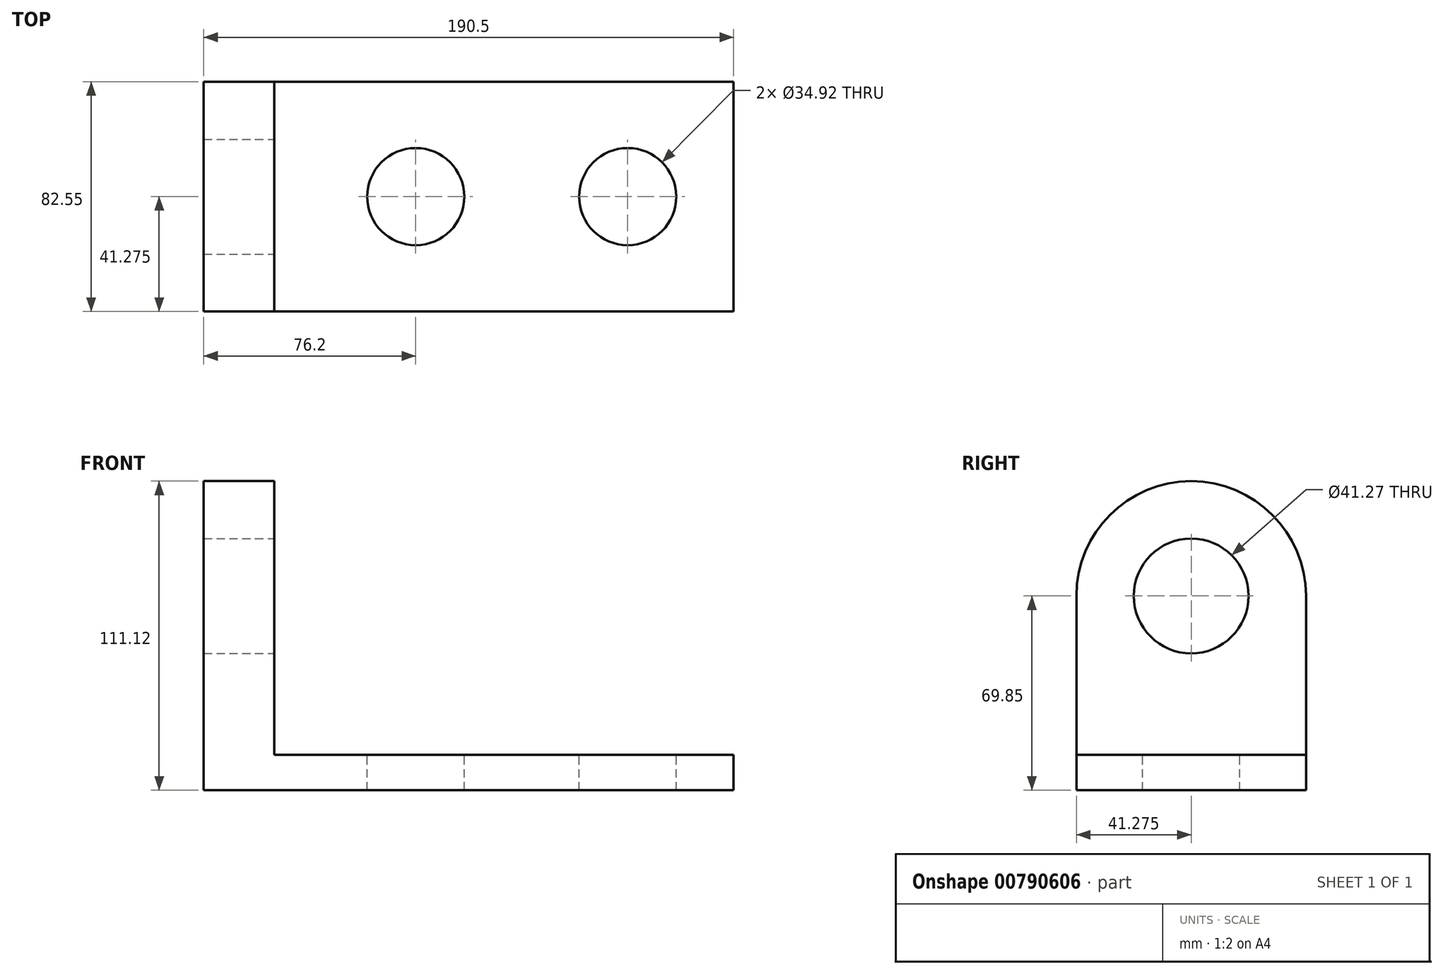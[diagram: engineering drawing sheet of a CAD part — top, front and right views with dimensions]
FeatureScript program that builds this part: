
annotation { "Feature Type Name" : "Feature", "Feature Type Description" : "" }
export const myFeature = defineFeature(function(context is Context, id is Id, definition is map)
    precondition{}
    {
        {
            var Q0;
            Q0=qCreatedBy(makeId("Front.planeOp"),FACE);
            var sketch = newSketch(context, id + "F0", { "sketchPlane" : qUnion([Q0])});
            skLineSegment(sketch, "E0", {"start": v(0, 0) * mm, "end": v(190.5, 0) * mm});
            skLineSegment(sketch, "E1", {"start": v(190.5, 0) * mm, "end": v(190.5, 12.7) * mm});
            skLineSegment(sketch, "E2", {"start": v(190.5, 12.7) * mm, "end": v(0, 12.7) * mm});
            skLineSegment(sketch, "E3", {"start": v(0, 12.7) * mm, "end": v(0, 0) * mm});
            skSolve(sketch);
        }
        {
            var Q0;
            Q0=makeQuery(id+"F0.imprint","IMPRINT",FACE,{"disambiguationData":[TD([[makeQuery(id+"F0.imprint","IMPRINT",EDGE,{"derivedFrom":sQuery(id+"F0.wireOp",EDGE,"E0")}),1.0]])]});
            extrude(context, id + "F1", {"entities" : qUnion([Q0]), "depth" : 82.55 * mm, "offsetDistance" : 25.4 * mm});
        }
        {
            var Q0;
            Q0=makeQuery(id+"F1.opExtrude","SWEPT_FACE",FACE,{"disambiguationData":[OSD([sQuery(id+"F0.wireOp",EDGE,"E2")])]});
            var sketch = newSketch(context, id + "F2", { "sketchPlane" : qUnion([Q0])});
            skLineSegment(sketch, "E4", {"start": v(190.5, -41.28) * mm, "end": v(152.4, -41.28) * mm, "construction": true});
            skLineSegment(sketch, "E5", {"start": v(152.4, -41.28) * mm, "end": v(76.2, -41.28) * mm, "construction": true});
            skCircle(sketch, "E6", {"center": v(76.2, -41.28) * mm, "radius": 17.46 * mm});
            skCircle(sketch, "E7", {"center": v(152.4, -41.28) * mm, "radius": 17.46 * mm});
            skSolve(sketch);
        }
        {
            var Q0;
            Q0=makeQuery(id+"F2.imprint","IMPRINT",FACE,{"disambiguationData":[TD([[makeQuery(id+"F2.imprint","IMPRINT",EDGE,{"derivedFrom":sQuery(id+"F2.wireOp",EDGE,"E6")}),1.0]])]});
            var Q1;
            Q1=makeQuery(id+"F2.imprint","IMPRINT",FACE,{"disambiguationData":[TD([[makeQuery(id+"F2.imprint","IMPRINT",EDGE,{"derivedFrom":sQuery(id+"F2.wireOp",EDGE,"E7")}),1.0]])]});
            extrude(context, id + "F3", {"entities" : qUnion([Q0, Q1]), "operationType" : NewBodyOperationType.REMOVE, "oppositeDirection" : true, "depth" : 25.4 * mm, "offsetDistance" : 25.4 * mm});
        }
        {
            var Q0;
            Q0=makeQuery(id+"F1.opExtrude","CAP_FACE",FACE,{"disambiguationData":[OSD([sQuery(id+"F0.wireOp",EDGE,"E0"),sQuery(id+"F0.wireOp",EDGE,"E1"),sQuery(id+"F0.wireOp",EDGE,"E2"),sQuery(id+"F0.wireOp",EDGE,"E3")])],"isStart":false});
            var sketch = newSketch(context, id + "F4", { "sketchPlane" : qUnion([Q0])});
            skLineSegment(sketch, "E8", {"start": v(0, 0) * mm, "end": v(25.4, 0) * mm});
            skLineSegment(sketch, "E9", {"start": v(0, 0) * mm, "end": v(0, 114.3) * mm});
            skLineSegment(sketch, "E10", {"start": v(25.4, 0) * mm, "end": v(25.4, 114.3) * mm});
            skLineSegment(sketch, "E11", {"start": v(25.4, 114.3) * mm, "end": v(0, 114.3) * mm});
            skSolve(sketch);
        }
        {
            var Q0;
            {var subQ3=sQuery(id+"F4.wireOp",EDGE,"E11");Q0=makeQuery(id+"F4.imprint","IMPRINT",FACE,{"disambiguationData":[TD([[makeQuery(id+"F4.imprint","IMPRINT",EDGE,{"derivedFrom":subQ3}),1.0]])]});}
            extrude(context, id + "F5", {"entities" : qUnion([Q0]), "operationType" : NewBodyOperationType.ADD, "oppositeDirection" : true, "depth" : 82.55 * mm, "offsetDistance" : 25.4 * mm});
        }
        {
            var Q0;
            Q0=makeQuery(id+"F5.opExtrude","SWEPT_FACE",FACE,{"disambiguationData":[OSD([sQuery(id+"F4.wireOp",EDGE,"E10")])]});
            var sketch = newSketch(context, id + "F6", { "sketchPlane" : qUnion([Q0])});
            skLineSegment(sketch, "E12", {"start": v(-82.55, 12.7) * mm, "end": v(-82.55, 69.85) * mm});
            skLineSegment(sketch, "E13", {"start": v(0, 12.7) * mm, "end": v(0, 69.85) * mm});
            skArc(sketch, "E14", {"start": v(0, 69.85) * mm, "mid": v(-41.28, 111.13) * mm, "end": v(-82.55, 69.85) * mm});
            skSolve(sketch);
        }
        {
            var Q0;
            {var subQ0=sQuery(id+"F6.wireOp",EDGE,"E14");Q0=makeQuery(id+"F6.imprint","IMPRINT",FACE,{"disambiguationData":[TD([[makeQuery(id+"F6.imprint","IMPRINT",EDGE,{"derivedFrom":subQ0}),-1.0]])]});}
            extrude(context, id + "F7", {"entities" : qUnion([Q0]), "operationType" : NewBodyOperationType.REMOVE, "oppositeDirection" : true, "depth" : 25.4 * mm, "offsetDistance" : 25.4 * mm});
        }
        {
            var Q0;
            Q0=makeQuery(id+"F5.opExtrude","SWEPT_FACE",FACE,{"disambiguationData":[OSD([sQuery(id+"F4.wireOp",EDGE,"E10")])]});
            var sketch = newSketch(context, id + "F8", { "sketchPlane" : qUnion([Q0])});
            skLineSegment(sketch, "E15", {"start": v(-82.55, 12.7) * mm, "end": v(-82.55, 69.85) * mm, "construction": true});
            skLineSegment(sketch, "E16", {"start": v(-82.55, 69.85) * mm, "end": v(-41.28, 69.85) * mm, "construction": true});
            skCircle(sketch, "E17", {"center": v(-41.28, 69.85) * mm, "radius": 20.64 * mm});
            skSolve(sketch);
        }
        {
            var Q0;
            Q0=makeQuery(id+"F8.imprint","IMPRINT",FACE,{"disambiguationData":[TD([[makeQuery(id+"F8.imprint","IMPRINT",EDGE,{"derivedFrom":sQuery(id+"F8.wireOp",EDGE,"E17")}),1.0]])]});
            extrude(context, id + "F9", {"entities" : qUnion([Q0]), "operationType" : NewBodyOperationType.REMOVE, "endBound" : BoundingType.THROUGH_ALL, "oppositeDirection" : true, "depth" : 25.4 * mm, "offsetDistance" : 25.4 * mm});
        }
    });
